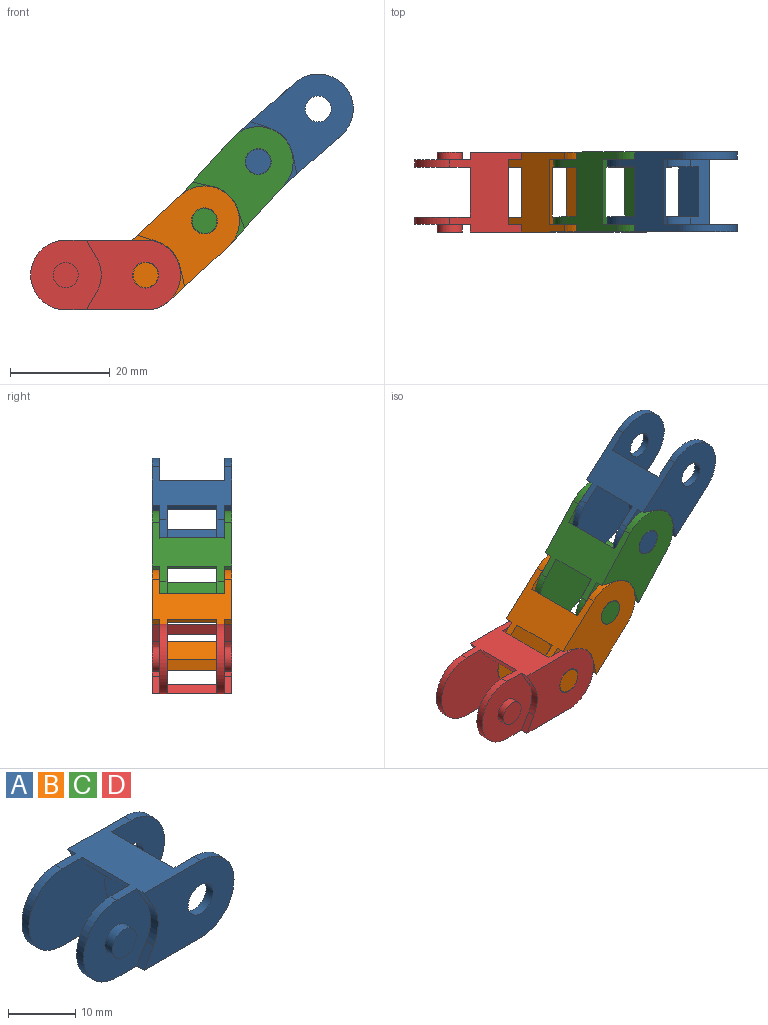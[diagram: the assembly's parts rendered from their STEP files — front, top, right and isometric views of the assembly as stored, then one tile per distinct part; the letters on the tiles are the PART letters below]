
ASSEMBLY  parts=4 mates=3
PART A: 34 faces, bbox 30x16x14 mm
  f0: plane 10x5.38mm, normal (0,0,1), area 53.8mm2, adj f10,f11,f14,f32
  f1: plane 10x5.38mm, normal (0,0,-1), area 53.8mm2, adj f10,f11,f12,f33
  f2: cylinder r=7mm len=14mm, axis (0,1,0), area 31.9mm2, adj f4,f5,f11,f22
  f3: cylinder r=7mm len=14mm, axis (0,1,0), area 31.9mm2, adj f4,f5,f10,f25
  f4: plane 16x16mm, normal (0,0,1), area 147.1mm2, adj f2,f3,f6,f7,f8,f9,f10,f11
  f5: plane 16x16mm, normal (0,0,-1), area 147.1mm2, adj f2,f3,f6,f7,f8,f9,f10,f11
  f6: plane 18.84x14mm, normal (0,-1,0), area 196mm2, adj f4,f5,f8,f18,f19,f20,f31
  f7: cylinder r=7mm len=14mm, axis (0,1,0), area 31.9mm2, adj f4,f5,f9,f17
  f8: cylinder r=7mm len=14mm, axis (0,1,0), area 31.9mm2, adj f4,f5,f6,f16
  f9: plane 18.84x14mm, normal (0,1,0), area 196mm2, adj f4,f5,f7,f24,f26,f27,f30
  f10: plane 17.69x14mm, normal (0,-1,0), area 191.1mm2, adj f0,f1,f3,f4,f5,f12,f13,f14
  f11: plane 17.69x14mm, normal (0,1,0), area 191.1mm2, adj f0,f1,f2,f4,f5,f12,f14,f15
  f12: plane 13.1x3.45mm, normal (0.87,0,-0.5), area 35.4mm2, adj f1,f4,f10,f11,f13,f15,f16,f17
  f13: cylinder r=7.1mm len=7.1mm, axis (0,1,0), area 11.5mm2, adj f10,f12,f14,f17
  f14: plane 13.1x3.45mm, normal (0.87,0,0.5), area 35.4mm2, adj f0,f5,f10,f11,f13,f15,f16,f17
  f15: cylinder r=7.1mm len=7.1mm, axis (0,1,0), area 11.5mm2, adj f11,f12,f14,f16
  f16: plane 14.1x14mm, normal (0,1,0), area 139.5mm2, adj f4,f5,f8,f12,f14,f15,f31
  f17: plane 14.1x14mm, normal (0,-1,0), area 139.5mm2, adj f4,f5,f7,f12,f13,f14,f30
  f18: plane 3.45x1.99mm, normal (-0.87,0,0.5), area 6.2mm2, adj f5,f6,f19,f22
  f19: cylinder r=7.1mm len=7.1mm, axis (0,-1,0), area 11.5mm2, adj f6,f18,f20,f22
  f20: plane 3.45x1.99mm, normal (-0.87,0,-0.5), area 6.2mm2, adj f4,f6,f19,f22
  f21: cylinder r=2.5mm len=5mm, axis (0,-1,0), area 24.3mm2, adj f22,f23
  f22: plane 14.1x14mm, normal (0,-1,0), area 141.1mm2, adj f2,f4,f5,f18,f19,f20,f21
  f23: plane 5x5mm, normal (0,-1,0), area 19.6mm2, adj f21
  f24: plane 3.45x1.99mm, normal (-0.87,0,0.5), area 6.2mm2, adj f5,f9,f25,f27
  f25: plane 14.1x14mm, normal (0,1,0), area 141.1mm2, adj f3,f4,f5,f24,f26,f27,f28
  f26: plane 3.45x1.99mm, normal (-0.87,0,-0.5), area 6.2mm2, adj f4,f9,f25,f27
  f27: cylinder r=7.1mm len=7.1mm, axis (0,1,0), area 11.5mm2, adj f9,f24,f25,f26
  f28: cylinder r=2.5mm len=5mm, axis (0,1,0), area 24.3mm2, adj f25,f29
  f29: plane 5x5mm, normal (0,1,0), area 19.6mm2, adj f28
  f30: cylinder r=2.6mm len=5.2mm, axis (0,-1,0), area 23.7mm2, adj f9,f17
  f31: cylinder r=2.6mm len=5.2mm, axis (0,-1,0), area 23.7mm2, adj f6,f16
  f32: plane 10x2mm, normal (-0.87,0,0.5), area 23.1mm2, adj f0,f5,f10,f11
  f33: plane 10x2mm, normal (-0.87,0,-0.5), area 23.1mm2, adj f1,f4,f10,f11
PART B: same geometry as A
PART C: same geometry as A
PART D: same geometry as A
PLACE A rot(axis=(0,-1,0),41.2deg) t=(36.53,0,27.96)mm
PLACE B rot(axis=(0,-1,0),42.6deg) t=(13.89,0,5.42)mm
PLACE C rot(axis=(0,-1,0),47.8deg) t=(25.15,0,16.76)mm
PLACE D at identity fixed
MATE revolute A.f21 <-> C.f30  axis (0,-1,0) through (30.52,-8,22.69)mm
MATE revolute C.f21 <-> B.f30  axis (0,-1,0) through (19.78,-8,10.83)mm
MATE revolute B.f21 <-> D.f7  axis (0,-1,0) through (8,-8,0)mm
